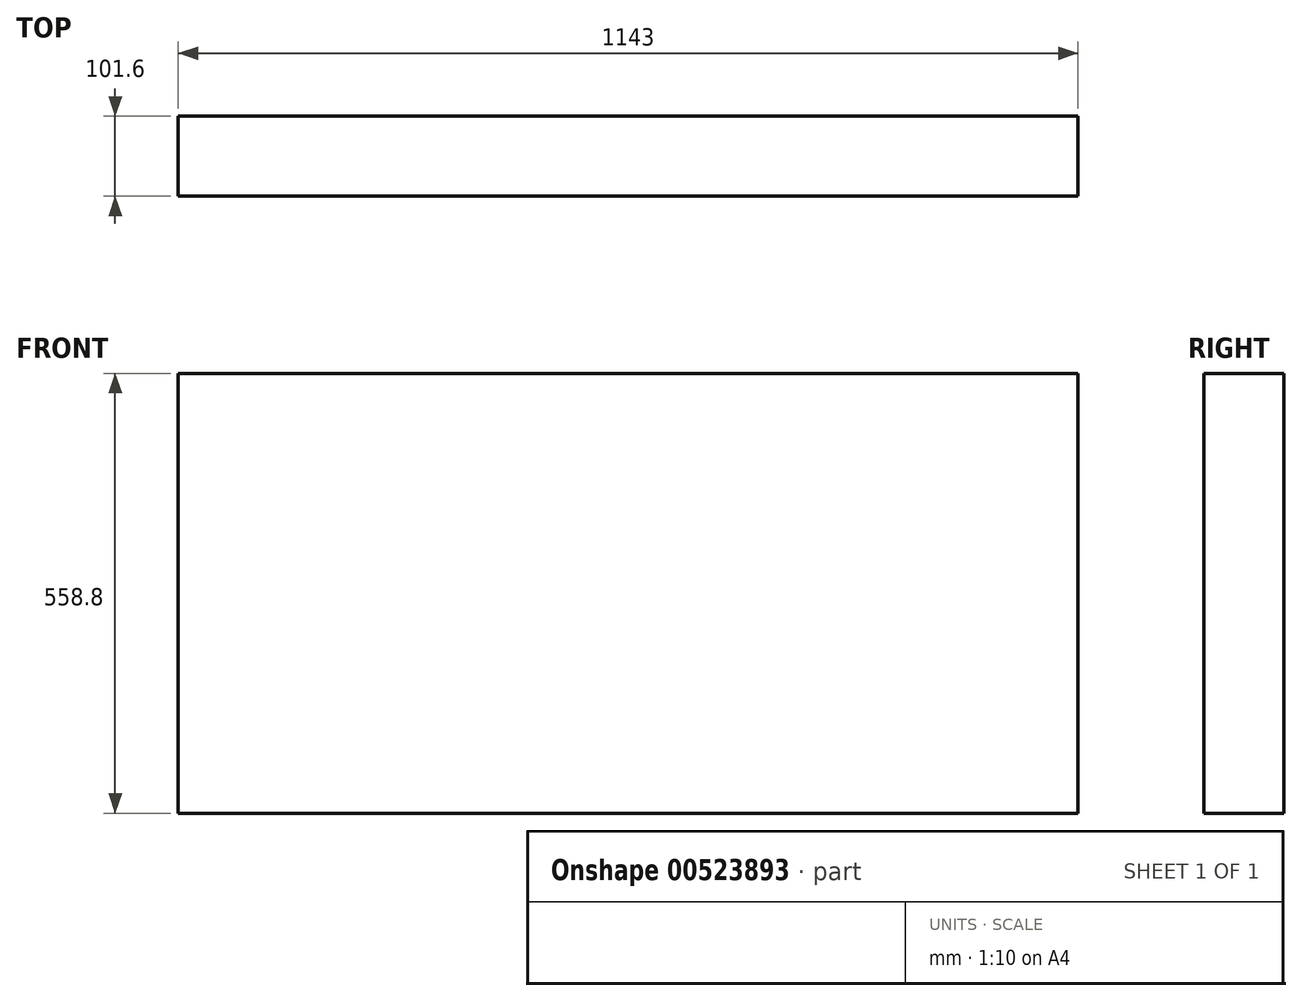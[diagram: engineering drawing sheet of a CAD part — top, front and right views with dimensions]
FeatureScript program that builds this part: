
annotation { "Feature Type Name" : "Feature", "Feature Type Description" : "" }
export const myFeature = defineFeature(function(context is Context, id is Id, definition is map)
    precondition{}
    {
        {
            var Q0;
            Q0=qCreatedBy(makeId("Front.planeOp"),FACE);
            var sketch = newSketch(context, id + "F0", { "sketchPlane" : qUnion([Q0])});
            skLineSegment(sketch, "E0.bottom", {"start": v(-571.5, 279.4) * mm, "end": v(571.5, 279.4) * mm});
            skLineSegment(sketch, "E0.top", {"start": v(-571.5, -279.4) * mm, "end": v(571.5, -279.4) * mm});
            skLineSegment(sketch, "E0.left", {"start": v(-571.5, 279.4) * mm, "end": v(-571.5, -279.4) * mm});
            skLineSegment(sketch, "E0.right", {"start": v(571.5, 279.4) * mm, "end": v(571.5, -279.4) * mm});
            skPoint(sketch, "E0.middle", {"position": v(0, 0) * mm});
            skSolve(sketch);
        }
        {
            var Q0;
            Q0 = qSketchRegion(id + "F0", true);
            extrude(context, id + "F1", {"entities" : qUnion([Q0]), "depth" : 101.6 * mm, "offsetDistance" : 25.4 * mm});
        }
    });
